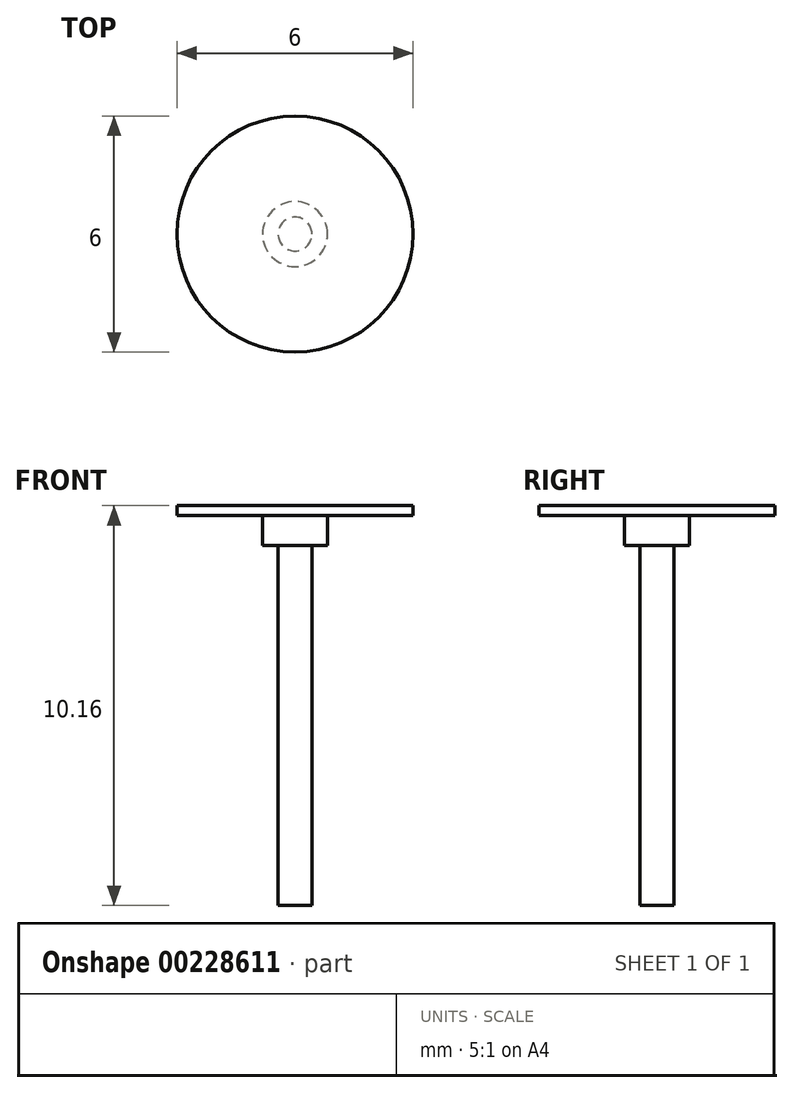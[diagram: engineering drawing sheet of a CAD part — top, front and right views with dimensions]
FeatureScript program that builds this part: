
annotation { "Feature Type Name" : "Feature", "Feature Type Description" : "" }
export const myFeature = defineFeature(function(context is Context, id is Id, definition is map)
    precondition{}
    {
        {
            var Q0;
            Q0=qCreatedBy(makeId("Front.planeOp"),FACE);
            var sketch = newSketch(context, id + "F0", { "sketchPlane" : qUnion([Q0])});
            skLineSegment(sketch, "E0", {"start": v(0, 0) * mm, "end": v(-3, 0) * mm});
            skLineSegment(sketch, "E1", {"start": v(-3, 0) * mm, "end": v(-3, -0.25) * mm});
            skLineSegment(sketch, "E2", {"start": v(-3, -0.25) * mm, "end": v(-0.83, -0.25) * mm});
            skLineSegment(sketch, "E3", {"start": v(-0.43, -1.02) * mm, "end": v(-0.43, -10.16) * mm});
            skLineSegment(sketch, "E4", {"start": v(-0.43, -10.16) * mm, "end": v(0, -10.16) * mm});
            skLineSegment(sketch, "E5", {"start": v(0, -10.16) * mm, "end": v(0, 0) * mm});
            skLineSegment(sketch, "E6", {"start": v(-0.43, -1.02) * mm, "end": v(-0.83, -1.02) * mm});
            skLineSegment(sketch, "E7", {"start": v(-0.83, -1.02) * mm, "end": v(-0.83, -0.25) * mm});
            skSolve(sketch);
        }
        {
            var Q0;
            Q0 = qSketchRegion(id + "F0", true);
            var Q1;
            Q1=sQuery(id+"F0.wireOp",EDGE,"E5");
            revolve(context, id + "F1", {"entities" : qUnion([Q0]), "axis" : qUnion([Q1]), "revolveType" : RevolveType.FULL});
        }
    });
